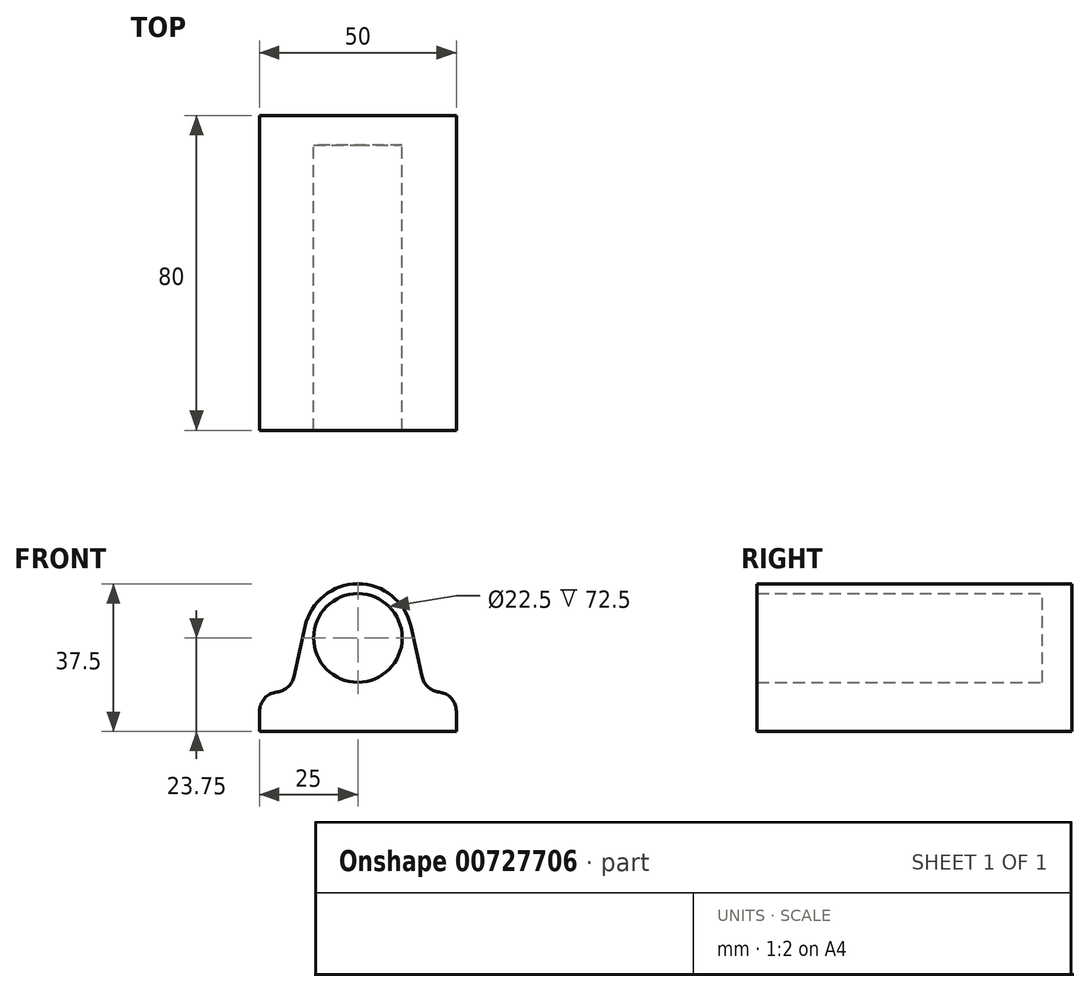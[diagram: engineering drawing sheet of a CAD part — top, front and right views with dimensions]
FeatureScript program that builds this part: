
annotation { "Feature Type Name" : "Feature", "Feature Type Description" : "" }
export const myFeature = defineFeature(function(context is Context, id is Id, definition is map)
    precondition{}
    {
        {
            var Q0;
            Q0=qCreatedBy(makeId("Front.planeOp"),FACE);
            var sketch = newSketch(context, id + "F0", { "sketchPlane" : qUnion([Q0])});
            skLineSegment(sketch, "E0", {"start": v(0, 0) * mm, "end": v(25, 0) * mm});
            skLineSegment(sketch, "E1", {"start": v(25, 0) * mm, "end": v(25, -10) * mm});
            skLineSegment(sketch, "E2", {"start": v(25, -10) * mm, "end": v(-25, -10) * mm});
            skLineSegment(sketch, "E3", {"start": v(-25, -10) * mm, "end": v(-25, 0) * mm});
            skLineSegment(sketch, "E4", {"start": v(-25, 0) * mm, "end": v(0, 0) * mm});
            skCircle(sketch, "E5", {"center": v(0, 13.75) * mm, "radius": 11.25 * mm});
            skCircle(sketch, "E6", {"center": v(0, 13.75) * mm, "radius": 13.75 * mm});
            skLineSegment(sketch, "E7", {"start": v(-13.43, 16.7) * mm, "end": v(-17.11, 0) * mm});
            skLineSegment(sketch, "E8", {"start": v(13.43, 16.7) * mm, "end": v(17.11, 0) * mm});
            skSolve(sketch);
        }
        {
            var Q0;
            Q0 = qSketchRegion(id + "F0", true);
            extrude(context, id + "F1", {"entities" : qUnion([Q0]), "depth" : 80 * mm, "offsetDistance" : 25 * mm});
        }
        {
            var Q0;
            Q0=makeQuery(id+"F0.imprint","IMPRINT",FACE,{"disambiguationData":[TD([[makeQuery(id+"F0.imprint","IMPRINT",EDGE,{"derivedFrom":sQuery(id+"F0.wireOp",EDGE,"E5")}),1.0]])]});
            extrude(context, id + "F2", {"entities" : qUnion([Q0]), "operationType" : NewBodyOperationType.ADD, "depth" : 7.5 * mm, "offsetDistance" : 25 * mm});
        }
        {
            var Q0;
            Q0=makeQuery(id+"F1.opExtrude","SWEPT_EDGE",EDGE,{"disambiguationData":[OSD([sQuery(id+"F0.wireOp",EDGE,"E4"),sQuery(id+"F0.wireOp",EDGE,"E7")])]});
            var Q1;
            Q1=makeQuery(id+"F1.opExtrude","SWEPT_EDGE",EDGE,{"disambiguationData":[OSD([sQuery(id+"F0.wireOp",EDGE,"E0"),sQuery(id+"F0.wireOp",EDGE,"E8")])]});
            fillet(context, id + "F3", {"entities" : qUnion([Q0, Q1]), "radius" : 5 * mm, "tangentPropagation" : true, "allowEdgeOverflow" : false});
        }
        {
            var Q0;
            Q0=makeQuery(id+"F1.opExtrude","SWEPT_EDGE",EDGE,{"disambiguationData":[OSD([sQuery(id+"F0.wireOp",EDGE,"E3"),sQuery(id+"F0.wireOp",EDGE,"E4")])]});
            var Q1;
            Q1=makeQuery(id+"F1.opExtrude","SWEPT_EDGE",EDGE,{"disambiguationData":[OSD([sQuery(id+"F0.wireOp",EDGE,"E0"),sQuery(id+"F0.wireOp",EDGE,"E1")])]});
            fillet(context, id + "F4", {"entities" : qUnion([Q0, Q1]), "radius" : 5 * mm, "tangentPropagation" : true, "allowEdgeOverflow" : false});
        }
    });
